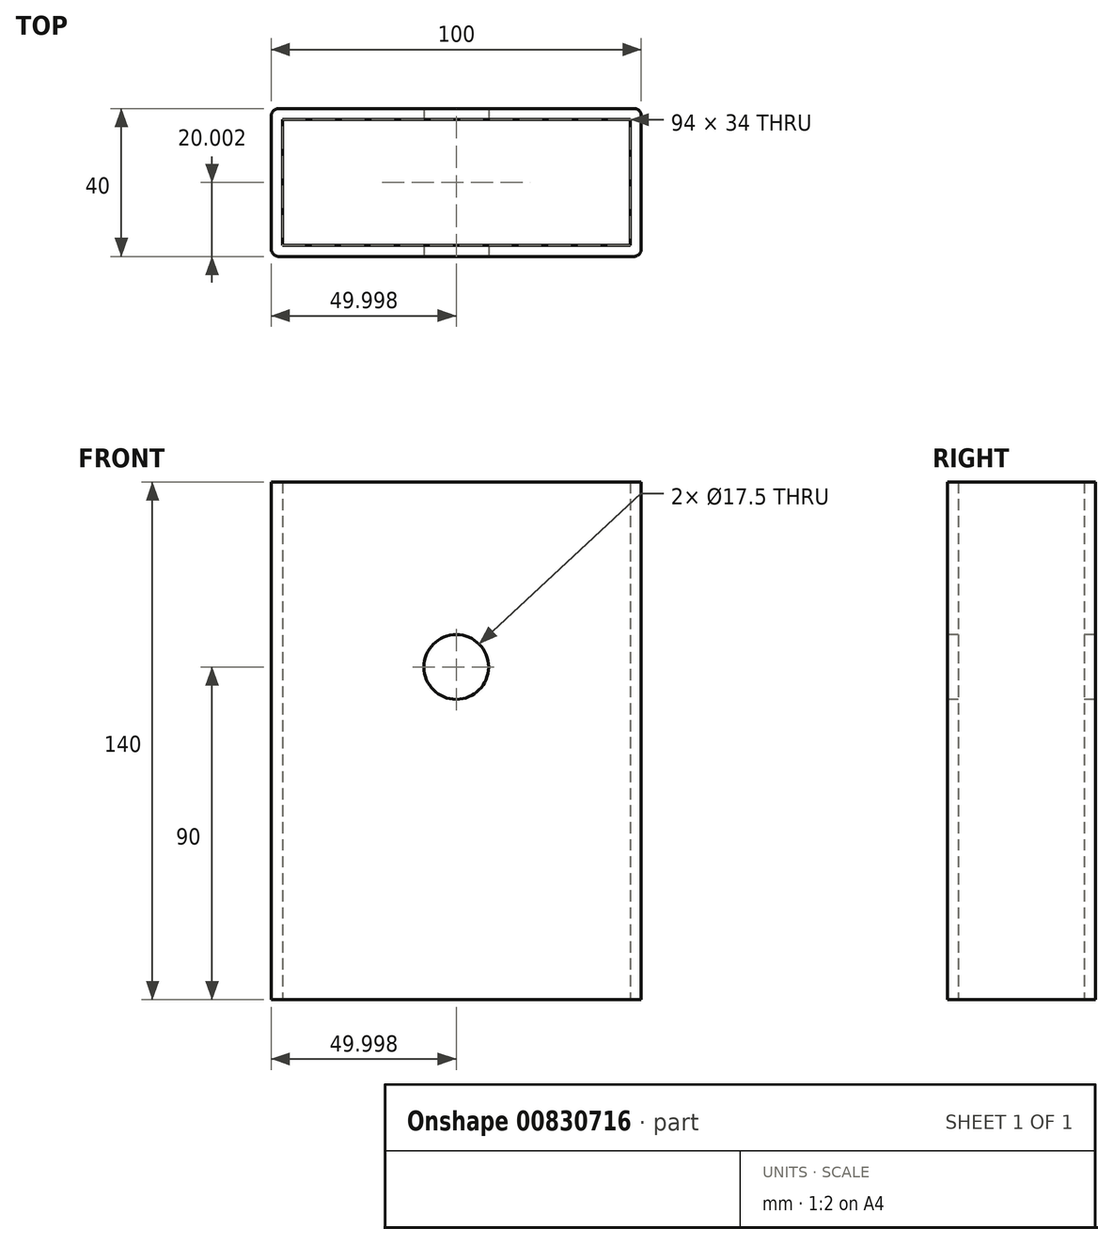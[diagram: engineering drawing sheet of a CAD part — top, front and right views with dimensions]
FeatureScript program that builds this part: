
annotation { "Feature Type Name" : "Feature", "Feature Type Description" : "" }
export const myFeature = defineFeature(function(context is Context, id is Id, definition is map)
    precondition{}
    {
        {
            assignVariable(context, id + "F0", {"name" : "TubeWidth", "anyValue" : 100});
        }
        {
            assignVariable(context, id + "F1", {"name" : "TubeHeight", "anyValue" : 40});
        }
        {
            assignVariable(context, id + "F2", {"name" : "MountHeight", "anyValue" : getVariable(context, 'TubeHeight') + getVariable(context, 'TubeWidth')});
        }
        {
            var Q0;
            Q0=qCreatedBy(makeId("Top.planeOp"),FACE);
            var sketch = newSketch(context, id + "F3", { "sketchPlane" : qUnion([Q0])});
            skPoint(sketch, "E0.middle", {"position": v(-14.96, 34.76) * mm});
            skLineSegment(sketch, "E1.bottom", {"start": v(-17.25, -51.74) * mm, "end": v(78.75, -51.74) * mm});
            skLineSegment(sketch, "E1.top", {"start": v(-17.25, -11.74) * mm, "end": v(78.75, -11.74) * mm});
            skLineSegment(sketch, "E1.left", {"start": v(-19.25, -49.74) * mm, "end": v(-19.25, -13.74) * mm});
            skLineSegment(sketch, "E1.right", {"start": v(80.75, -49.74) * mm, "end": v(80.75, -13.74) * mm});
            skPoint(sketch, "E2.visualSharp", {"position": v(-19.25, -11.74) * mm});
            skArc(sketch, "E2.filletArc", {"start": v(-17.25, -11.74) * mm, "mid": v(-18.67, -12.32) * mm, "end": v(-19.25, -13.74) * mm});
            skPoint(sketch, "E3.visualSharp", {"position": v(80.75, -11.74) * mm});
            skArc(sketch, "E3.filletArc", {"start": v(80.75, -13.74) * mm, "mid": v(80.16, -12.32) * mm, "end": v(78.75, -11.74) * mm});
            skPoint(sketch, "E4.visualSharp", {"position": v(80.75, -51.74) * mm});
            skArc(sketch, "E4.filletArc", {"start": v(78.75, -51.74) * mm, "mid": v(80.16, -51.15) * mm, "end": v(80.75, -49.74) * mm});
            skPoint(sketch, "E5.visualSharp", {"position": v(-19.25, -51.74) * mm});
            skArc(sketch, "E5.filletArc", {"start": v(-19.25, -49.74) * mm, "mid": v(-18.67, -51.15) * mm, "end": v(-17.25, -51.74) * mm});
            skLineSegment(sketch, "E6.0", {"start": v(-17.25, 46.26) * mm, "end": v(-17.25, 46.26) * mm});
            skLineSegment(sketch, "E6.2", {"start": v(-17.25, -49.74) * mm, "end": v(-17.25, -49.74) * mm});
            skLineSegment(sketch, "E6.4", {"start": v(18.75, -49.74) * mm, "end": v(18.75, -49.74) * mm});
            skLineSegment(sketch, "E6.7", {"start": v(18.75, 46.26) * mm, "end": v(18.75, 46.26) * mm});
            skLineSegment(sketch, "E7.0", {"start": v(77.75, -48.74) * mm, "end": v(77.75, -14.74) * mm});
            skLineSegment(sketch, "E7.1", {"start": v(-16.25, -48.74) * mm, "end": v(77.75, -48.74) * mm});
            skLineSegment(sketch, "E7.2", {"start": v(-16.25, -48.74) * mm, "end": v(-16.25, -14.74) * mm});
            skLineSegment(sketch, "E7.3", {"start": v(-16.25, -14.74) * mm, "end": v(77.75, -14.74) * mm});
            skSolve(sketch);
        }
        {
            var Q0;
            Q0 = qSketchRegion(id + "F3", true);
            extrude(context, id + "F4", {"entities" : qUnion([Q0]), "depth" : (getVariable(context, 'MountHeight')) * mm, "offsetDistance" : 25 * mm});
        }
        {
            var Q0;
            Q0=makeQuery(id+"F4.opExtrude","SWEPT_FACE",FACE,{"disambiguationData":[OSD([sQuery(id+"F3.wireOp",EDGE,"E1.bottom")])]});
            var sketch = newSketch(context, id + "F5", { "sketchPlane" : qUnion([Q0])});
            skPoint(sketch, "E8", {"position": v(30.75, 90) * mm});
            skPoint(sketch, "E8.positionSnap0", {"position": v(30.75, 140) * mm});
            skLineSegment(sketch, "E9", {"start": v(30.75, 140) * mm, "end": v(30.75, 90) * mm});
            skSolve(sketch);
        }
        {
            var Q0;
            Q0=sQuery(id+"F5.wireOp",VERTEX,"E8");
            var Q1;
            Q1=makeQuery(id+"F4.opExtrude","SWEPT_BODY",BODY,{"disambiguationData":[OSD([sQuery(id+"F3.wireOp",EDGE,"E1.bottom"),sQuery(id+"F3.wireOp",EDGE,"E1.top"),sQuery(id+"F3.wireOp",EDGE,"E1.left"),sQuery(id+"F3.wireOp",EDGE,"E1.right"),sQuery(id+"F3.wireOp",EDGE,"E2.filletArc"),sQuery(id+"F3.wireOp",EDGE,"E3.filletArc"),sQuery(id+"F3.wireOp",EDGE,"E4.filletArc"),sQuery(id+"F3.wireOp",EDGE,"E5.filletArc"),sQuery(id+"F3.wireOp",EDGE,"E7.0"),sQuery(id+"F3.wireOp",EDGE,"E7.1"),sQuery(id+"F3.wireOp",EDGE,"E7.2"),sQuery(id+"F3.wireOp",EDGE,"E7.3")])]});
            hole(context, id + "F6", {"style" : HoleStyle.SIMPLE, "endStyle" : HoleEndStyle.THROUGH, "standardTappedOrClearance" : lookupTablePath({ "fit" : "Normal", "standard" : "ISO", "size" : "M16", "type" : "Clearance" }), "standardBlindInLast" : lookupTablePath({ "fit" : "Standard", "standard" : "ISO", "size" : "M16", "type" : "Clearance" }), "holeDiameter" : 17.5 * mm, "majorDiameter" : 5 * mm, "isTappedThrough" : true, "tappedDepth" : 12 * mm, "tapClearance" : 3, "startFromSketch" : true, "locations" : qUnion([Q0]), "scope" : qUnion([Q1])});
        }
    });
